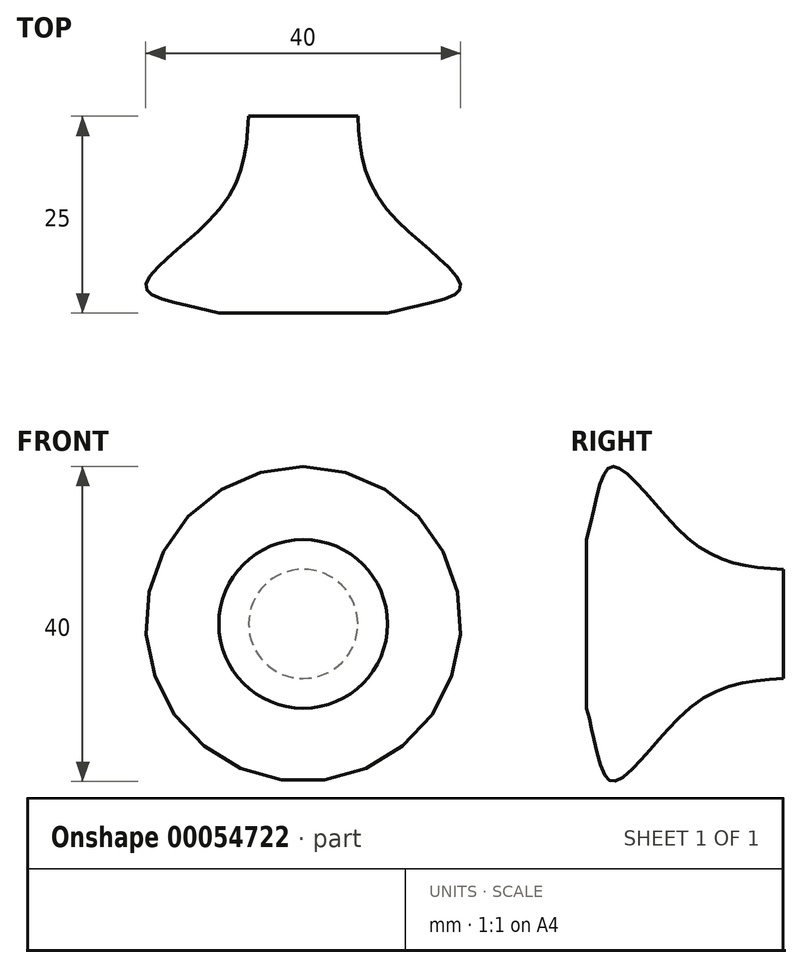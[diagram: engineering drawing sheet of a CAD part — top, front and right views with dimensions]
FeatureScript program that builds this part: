
annotation { "Feature Type Name" : "Feature", "Feature Type Description" : "" }
export const myFeature = defineFeature(function(context is Context, id is Id, definition is map)
    precondition{}
    {
        {
            var Q0;
            Q0=qCreatedBy(makeId("Top.planeOp"),FACE);
            var sketch = newSketch(context, id + "F0", { "sketchPlane" : qUnion([Q0])});
            skLineSegment(sketch, "E0", {"start": v(0, 0) * mm, "end": v(0, -25) * mm});
            skLineSegment(sketch, "E1", {"start": v(0, -25) * mm, "end": v(-10.72, -25) * mm});
            skFitSpline(sketch, "E2", {"points": [v(-10.72, -25) * mm, v(-20, -21.63) * mm, v(-10.72, -11.93) * mm, v(-6.93, 0) * mm], "startDerivative": vector(-45.84, 12.57) * mm, "endDerivative": vector(2.12, 39.38) * mm});
            skLineSegment(sketch, "E3", {"start": v(-6.93, 0) * mm, "end": v(0, 0) * mm});
            skSolve(sketch);
        }
        {
            var Q0;
            Q0=makeQuery(id+"F0.imprint","IMPRINT",FACE,{"disambiguationData":[TD([[makeQuery(id+"F0.imprint","IMPRINT",EDGE,{"derivedFrom":sQuery(id+"F0.wireOp",EDGE,"E0")}),-1.0]])]});
            var Q1;
            Q1=sQuery(id+"F0.wireOp",EDGE,"E0");
            revolve(context, id + "F1", {"entities" : qUnion([Q0]), "axis" : qUnion([Q1]), "revolveType" : RevolveType.FULL});
        }
    });
